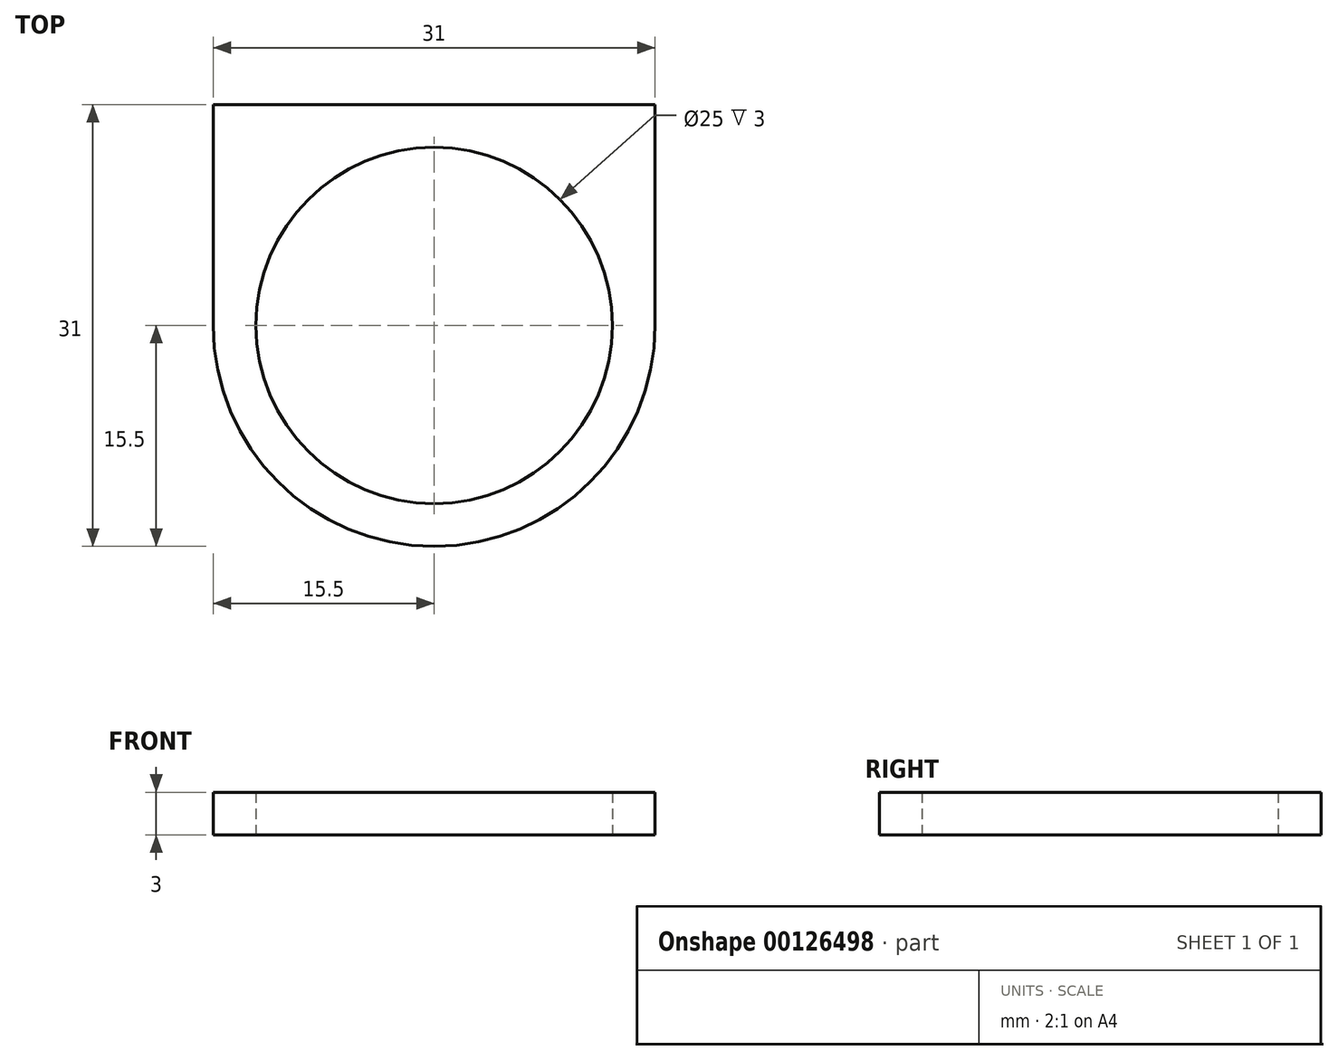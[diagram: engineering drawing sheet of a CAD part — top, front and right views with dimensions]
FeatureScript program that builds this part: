
annotation { "Feature Type Name" : "Feature", "Feature Type Description" : "" }
export const myFeature = defineFeature(function(context is Context, id is Id, definition is map)
    precondition{}
    {
        {
            var Q0;
            Q0=qCreatedBy(makeId("Top.planeOp"),FACE);
            var sketch = newSketch(context, id + "F0", { "sketchPlane" : qUnion([Q0])});
            skCircle(sketch, "E0", {"center": v(0, 0) * mm, "radius": 12.5 * mm});
            skArc(sketch, "E1.0", {"start": v(-15.5, 0) * mm, "mid": v(0, -15.5) * mm, "end": v(15.5, 0) * mm});
            skLineSegment(sketch, "E2", {"start": v(-15.5, 0) * mm, "end": v(-15.5, 15.5) * mm});
            skLineSegment(sketch, "E3", {"start": v(15.5, 0) * mm, "end": v(15.5, 15.5) * mm});
            skPoint(sketch, "E4.start.orphan", {"position": v(0, 15.5) * mm});
            skLineSegment(sketch, "E5", {"start": v(0, 0) * mm, "end": v(0, 24.6) * mm, "construction": true});
            skLineSegment(sketch, "E6", {"start": v(0, 15.5) * mm, "end": v(-12.5, 15.5) * mm});
            skLineSegment(sketch, "E7", {"start": v(0, 15.5) * mm, "end": v(12.5, 15.5) * mm});
            skLineSegment(sketch, "E8", {"start": v(-15.5, 15.5) * mm, "end": v(-12.5, 15.5) * mm});
            skLineSegment(sketch, "E9", {"start": v(15.5, 15.5) * mm, "end": v(12.5, 15.5) * mm});
            skSolve(sketch);
        }
        {
            var Q0;
            Q0=qSketchRegion(id+"F0",true);
            extrude(context, id + "F1", {"entities" : qUnion([Q0]), "endBound" : BoundingType.SYMMETRIC, "depth" : 3 * mm});
        }
    });
